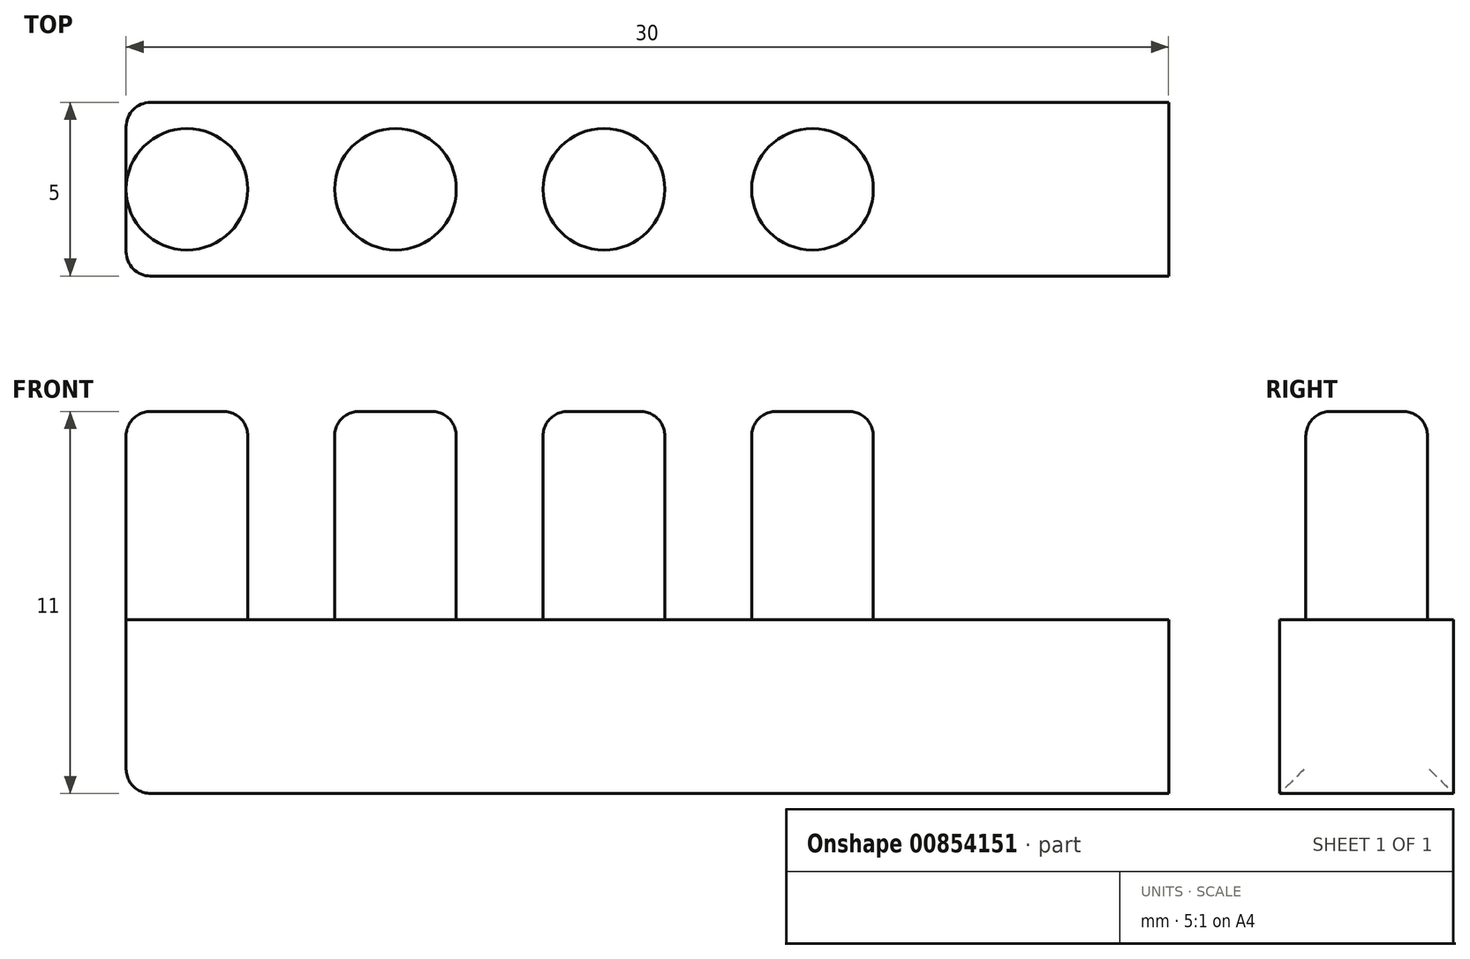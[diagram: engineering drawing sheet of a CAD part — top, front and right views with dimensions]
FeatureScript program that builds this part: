
annotation { "Feature Type Name" : "Feature", "Feature Type Description" : "" }
export const myFeature = defineFeature(function(context is Context, id is Id, definition is map)
    precondition{}
    {
        {
            var Q0;
            Q0=qCreatedBy(makeId("Top.planeOp"),FACE);
            var sketch = newSketch(context, id + "F0", { "sketchPlane" : qUnion([Q0])});
            skLineSegment(sketch, "E0.bottom", {"start": v(17.52, -2.5) * mm, "end": v(-12.48, -2.5) * mm});
            skLineSegment(sketch, "E0.top", {"start": v(17.52, 2.5) * mm, "end": v(-12.48, 2.5) * mm});
            skLineSegment(sketch, "E0.left", {"start": v(17.52, -2.5) * mm, "end": v(17.52, 2.5) * mm});
            skLineSegment(sketch, "E0.right", {"start": v(-12.48, -2.5) * mm, "end": v(-12.48, 2.5) * mm});
            skPoint(sketch, "E0.middle", {"position": v(2.52, 0) * mm});
            skLineSegment(sketch, "E1.bottom", {"start": v(-12.48, 2.5) * mm, "end": v(-5.23, 2.5) * mm, "construction": true});
            skLineSegment(sketch, "E1.top", {"start": v(-12.48, 0) * mm, "end": v(-5.23, 0) * mm, "construction": true});
            skLineSegment(sketch, "E1.left", {"start": v(-12.48, 2.5) * mm, "end": v(-12.48, 0) * mm, "construction": true});
            skLineSegment(sketch, "E2.bottom", {"start": v(-5.23, 2.5) * mm, "end": v(-1.73, 2.5) * mm, "construction": true});
            skLineSegment(sketch, "E2.top", {"start": v(-5.23, 0) * mm, "end": v(-1.73, 0) * mm, "construction": true});
            skLineSegment(sketch, "E3.bottom", {"start": v(-1.73, 2.5) * mm, "end": v(1.52, 2.5) * mm, "construction": true});
            skLineSegment(sketch, "E3.top", {"start": v(-1.73, 0) * mm, "end": v(1.52, 0) * mm, "construction": true});
            skLineSegment(sketch, "E3.right", {"start": v(1.52, 2.5) * mm, "end": v(1.52, 0) * mm, "construction": true});
            skLineSegment(sketch, "E4.bottom", {"start": v(1.52, 2.5) * mm, "end": v(17.52, 2.5) * mm, "construction": true});
            skLineSegment(sketch, "E4.top", {"start": v(1.52, 0) * mm, "end": v(17.52, 0) * mm, "construction": true});
            skLineSegment(sketch, "E4.right", {"start": v(17.52, 2.5) * mm, "end": v(17.52, 0) * mm, "construction": true});
            skSolve(sketch);
        }
        {
            var Q0;
            Q0=makeQuery(id+"F0.imprint","IMPRINT",FACE,{"disambiguationData":[TD([[makeQuery(id+"F0.imprint","IMPRINT",EDGE,{"derivedFrom":sQuery(id+"F0.wireOp",EDGE,"E0.bottom")}),-1.0]])]});
            extrude(context, id + "F1", {"entities" : qUnion([Q0]), "depth" : 5 * mm, "offsetDistance" : 25 * mm});
        }
        {
            var Q0;
            Q0=makeQuery(id+"F1.opExtrude","CAP_FACE",FACE,{"disambiguationData":[OSD([sQuery(id+"F0.wireOp",EDGE,"E0.bottom"),sQuery(id+"F0.wireOp",EDGE,"E0.top"),sQuery(id+"F0.wireOp",EDGE,"E0.left"),sQuery(id+"F0.wireOp",EDGE,"E0.right")])],"isStart":false});
            var sketch = newSketch(context, id + "F2", { "sketchPlane" : qUnion([Q0])});
            skLineSegment(sketch, "E5", {"start": v(17.52, 0) * mm, "end": v(7.27, 0) * mm, "construction": true});
            skPoint(sketch, "E5.endSnap0", {"position": v(17.52, 0) * mm});
            skLineSegment(sketch, "E6", {"start": v(7.27, 0) * mm, "end": v(4.27, 0) * mm, "construction": true});
            skCircle(sketch, "E7", {"center": v(4.27, 0) * mm, "radius": 1.5 * mm, "construction": true});
            skCircle(sketch, "E8", {"center": v(7.27, 0) * mm, "radius": 1.75 * mm});
            skLineSegment(sketch, "E9", {"start": v(4.27, 0) * mm, "end": v(1.27, 0) * mm, "construction": true});
            skLineSegment(sketch, "E10", {"start": v(1.27, 0) * mm, "end": v(-1.73, 0) * mm, "construction": true});
            skLineSegment(sketch, "E11", {"start": v(-1.73, 0) * mm, "end": v(-4.73, 0) * mm, "construction": true});
            skCircle(sketch, "E12", {"center": v(1.27, 0) * mm, "radius": 1.75 * mm});
            skCircle(sketch, "E13", {"center": v(-1.73, 0) * mm, "radius": 1.5 * mm, "construction": true});
            skCircle(sketch, "E14", {"center": v(-4.73, 0) * mm, "radius": 1.75 * mm});
            skLineSegment(sketch, "E15", {"start": v(-4.73, 0) * mm, "end": v(-7.73, 0) * mm, "construction": true});
            skLineSegment(sketch, "E16", {"start": v(-7.73, 0) * mm, "end": v(-10.73, 0) * mm, "construction": true});
            skCircle(sketch, "E17", {"center": v(-10.73, 0) * mm, "radius": 1.75 * mm});
            skCircle(sketch, "E18", {"center": v(-7.73, 0) * mm, "radius": 1.5 * mm, "construction": true});
            skSolve(sketch);
        }
        {
            var Q0;
            Q0=makeQuery(id+"F2.imprint","IMPRINT",FACE,{"disambiguationData":[TD([[makeQuery(id+"F2.imprint","IMPRINT",EDGE,{"derivedFrom":sQuery(id+"F2.wireOp",EDGE,"E8")}),1.0]])]});
            var Q1;
            Q1=makeQuery(id+"F2.imprint","IMPRINT",FACE,{"disambiguationData":[TD([[makeQuery(id+"F2.imprint","IMPRINT",EDGE,{"derivedFrom":sQuery(id+"F2.wireOp",EDGE,"E12")}),1.0]])]});
            var Q2;
            {var subQ0=sQuery(id+"F2.wireOp",EDGE,"E13");var subQ1=sQuery(id+"F2.wireOp",EDGE,"E12");var subQ2=makeQuery(id+"F2.imprint","INTERSECT",VERTEX,{"disambiguationData":[OD(0.0)],"derivedFrom":[subQ1,subQ0]});Q2=makeQuery(id+"F2.imprint","IMPRINT",FACE,{"disambiguationData":[TD([[makeQuery(id+"F2.imprint","IMPRINT",EDGE,{"disambiguationData":[TD([[subQ2,-1.0]])],"derivedFrom":subQ1}),1.0]])]});}
            var Q3;
            {var subQ0=sQuery(id+"F2.wireOp",EDGE,"E14");var subQ1=makeQuery(id+"F2.imprint","INTERSECT",VERTEX,{"derivedFrom":[sQuery(id+"F2.wireOp",EDGE,"E13"),subQ0]});Q3=makeQuery(id+"F2.imprint","IMPRINT",FACE,{"disambiguationData":[TD([[makeQuery(id+"F2.imprint","IMPRINT",EDGE,{"disambiguationData":[TD([[subQ1,-1.0]])],"derivedFrom":subQ0}),1.0]])]});}
            var Q4;
            {var subQ0=sQuery(id+"F2.wireOp",EDGE,"E18");var subQ1=sQuery(id+"F2.wireOp",EDGE,"E17");var subQ2=makeQuery(id+"F2.imprint","INTERSECT",VERTEX,{"disambiguationData":[OD(0.0)],"derivedFrom":[subQ1,subQ0]});Q4=makeQuery(id+"F2.imprint","IMPRINT",FACE,{"disambiguationData":[TD([[makeQuery(id+"F2.imprint","IMPRINT",EDGE,{"disambiguationData":[TD([[subQ2,-1.0]])],"derivedFrom":subQ1}),1.0]])]});}
            var Q5;
            {var subQ0=sQuery(id+"F2.wireOp",EDGE,"E14");var subQ1=sQuery(id+"F2.wireOp",EDGE,"E13");var subQ2=makeQuery(id+"F2.imprint","INTERSECT",VERTEX,{"disambiguationData":[OD(0.0)],"derivedFrom":[subQ1,subQ0]});Q5=makeQuery(id+"F2.imprint","IMPRINT",FACE,{"disambiguationData":[TD([[makeQuery(id+"F2.imprint","IMPRINT",EDGE,{"disambiguationData":[TD([[subQ2,-1.0]])],"derivedFrom":subQ1}),-1.0]])]});}
            var Q6;
            {var subQ0=sQuery(id+"F2.wireOp",EDGE,"E12");var subQ1=sQuery(id+"F2.wireOp",EDGE,"E7");var subQ2=makeQuery(id+"F2.imprint","INTERSECT",VERTEX,{"disambiguationData":[OD(0.0)],"derivedFrom":[subQ1,subQ0]});Q6=makeQuery(id+"F2.imprint","IMPRINT",FACE,{"disambiguationData":[TD([[makeQuery(id+"F2.imprint","IMPRINT",EDGE,{"disambiguationData":[TD([[subQ2,-1.0]])],"derivedFrom":subQ1}),1.0]])]});}
            var Q7;
            Q7=makeQuery(id+"F2.imprint","IMPRINT",FACE,{"disambiguationData":[TD([[makeQuery(id+"F2.imprint","IMPRINT",EDGE,{"derivedFrom":sQuery(id+"F2.wireOp",EDGE,"E14")}),1.0]])]});
            extrude(context, id + "F3", {"entities" : qUnion([Q0, Q1, Q2, Q3, Q4, Q5, Q6, Q7]), "operationType" : NewBodyOperationType.ADD, "depth" : 6 * mm, "offsetDistance" : 25 * mm});
        }
        {
            var Q0;
            Q0=makeQuery(id+"F3.opExtrude","CAP_FACE",FACE,{"disambiguationData":[OSD([sQuery(id+"F2.wireOp",EDGE,"E7")])],"isStart":false});
            var Q1;
            Q1=makeQuery(id+"F3.opExtrude","CAP_FACE",FACE,{"disambiguationData":[OSD([sQuery(id+"F2.wireOp",EDGE,"E8")])],"isStart":false});
            var Q2;
            Q2=makeQuery(id+"F1.opExtrude","CAP_EDGE",EDGE,{"disambiguationData":[OSD([sQuery(id+"F0.wireOp",EDGE,"E0.right")])],"isStart":true});
            var Q3;
            Q3=makeQuery(id+"F3.opExtrude","CAP_FACE",FACE,{"disambiguationData":[OSD([sQuery(id+"F2.wireOp",EDGE,"E12")])],"isStart":false});
            var Q4;
            Q4=makeQuery(id+"F3.opExtrude","CAP_FACE",FACE,{"disambiguationData":[OSD([sQuery(id+"F2.wireOp",EDGE,"E13")])],"isStart":false});
            var Q5;
            Q5=makeQuery(id+"F3.opExtrude","CAP_FACE",FACE,{"disambiguationData":[OSD([sQuery(id+"F2.wireOp",EDGE,"E14")])],"isStart":false});
            var Q6;
            Q6=makeQuery(id+"F1.opExtrude","SWEPT_EDGE",EDGE,{"disambiguationData":[OSD([sQuery(id+"F0.wireOp",EDGE,"E0.top"),sQuery(id+"F0.wireOp",EDGE,"E0.right")])]});
            var Q7;
            Q7=makeQuery(id+"F1.opExtrude","SWEPT_EDGE",EDGE,{"disambiguationData":[OSD([sQuery(id+"F0.wireOp",EDGE,"E0.bottom"),sQuery(id+"F0.wireOp",EDGE,"E0.right")])]});
            var Q8;
            Q8=makeQuery(id+"F3.opExtrude","CAP_FACE",FACE,{"disambiguationData":[OSD([sQuery(id+"F2.wireOp",EDGE,"E17")])],"isStart":false});
            fillet(context, id + "F4", {"entities" : qUnion([Q0, Q1, Q2, Q3, Q4, Q5, Q6, Q7, Q8]), "radius" : .7 * mm, "tangentPropagation" : true, "allowEdgeOverflow" : false});
        }
    });
